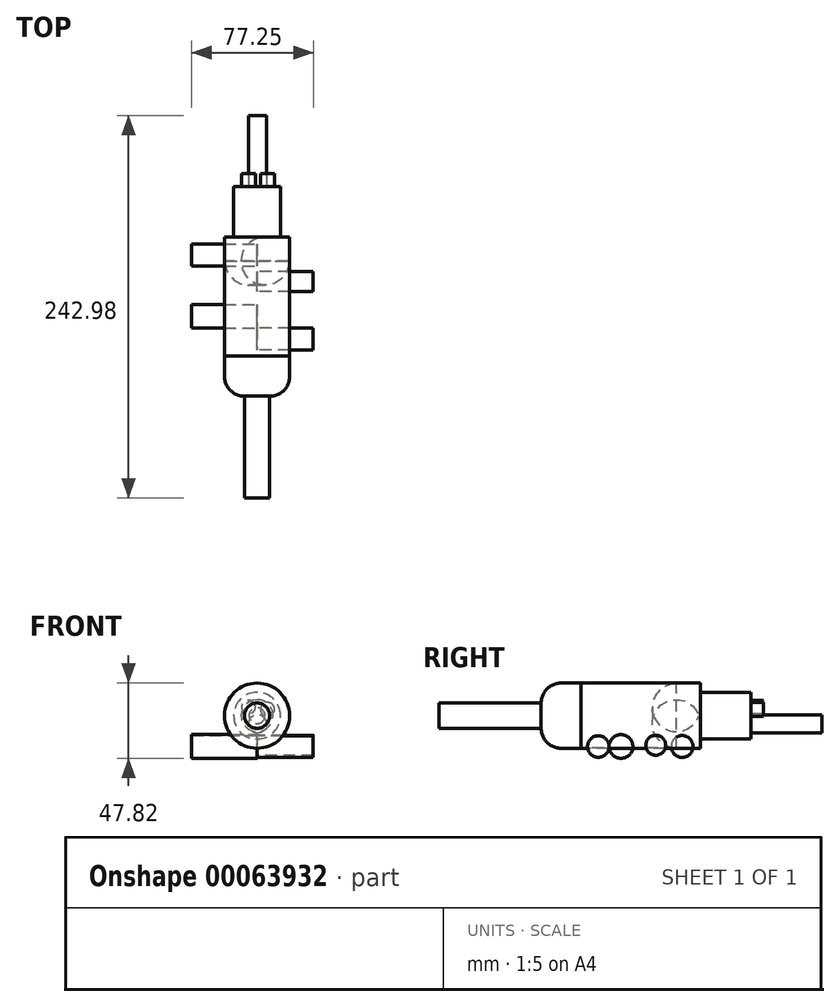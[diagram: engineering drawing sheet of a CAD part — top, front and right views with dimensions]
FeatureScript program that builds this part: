
annotation { "Feature Type Name" : "Feature", "Feature Type Description" : "" }
export const myFeature = defineFeature(function(context is Context, id is Id, definition is map)
    precondition{}
    {
        {
            var Q0;
            Q0=qCreatedBy(makeId("Front.planeOp"),FACE);
            var sketch = newSketch(context, id + "F0", { "sketchPlane" : qUnion([Q0])});
            skCircle(sketch, "E0", {"center": v(0, 0) * mm, "radius": 20.71 * mm});
            skSolve(sketch);
        }
        {
            var Q0;
            Q0 = qSketchRegion(id + "F0", true);
            extrude(context, id + "F1", {"entities" : qUnion([Q0]), "depth" : 25.4 * mm});
        }
        {
            var Q0;
            Q0=makeQuery(id+"F1.opExtrude","CAP_EDGE",EDGE,{"disambiguationData":[OSD([sQuery(id+"F0.wireOp",EDGE,"E0")])],"isStart":false});
            fillet(context, id + "F2", {"entities" : qUnion([Q0]), "radius" : 12.7 * mm, "tangentPropagation" : true, "allowEdgeOverflow" : false});
        }
        {
            var Q0;
            Q0=makeQuery(id+"F1.opExtrude","CAP_FACE",FACE,{"disambiguationData":[OSD([sQuery(id+"F0.wireOp",EDGE,"E0")])],"isStart":false});
            extrude(context, id + "F3", {"entities" : qUnion([Q0]), "depth" : 64.69 * mm});
        }
        {
            var Q0;
            Q0=qCreatedBy(makeId("Front.planeOp"),FACE);
            var sketch = newSketch(context, id + "F4", { "sketchPlane" : qUnion([Q0])});
            skCircle(sketch, "E1", {"center": v(0, 0) * mm, "radius": 20.32 * mm});
            skSolve(sketch);
        }
        {
            var Q0;
            Q0 = qSketchRegion(id + "F4", true);
            var Q1;
            Q1=makeQuery(id+"F1.opExtrude","CAP_FACE",FACE,{"disambiguationData":[OSD([sQuery(id+"F0.wireOp",EDGE,"E0")])],"isStart":true});
            extrude(context, id + "F5", {"entities" : qUnion([Q0, Q1]), "oppositeDirection" : true, "depth" : 75.69 * mm});
        }
        {
            var Q0;
            Q0=makeQuery(id+"F5.opExtrude","CAP_EDGE",EDGE,{"disambiguationData":[OSD([sQuery(id+"F4.wireOp",EDGE,"E1")])],"isStart":false});
            fillet(context, id + "F6", {"entities" : qUnion([Q0]), "radius" : 15.24 * mm, "tangentPropagation" : true, "allowEdgeOverflow" : false});
        }
        {
            var Q0;
            Q0=makeQuery(id+"F5.opExtrude","CAP_FACE",FACE,{"disambiguationData":[OSD([sQuery(id+"F0.wireOp",EDGE,"E0")])],"isStart":false});
            var sketch = newSketch(context, id + "F7", { "sketchPlane" : qUnion([Q0])});
            skCircle(sketch, "E2", {"center": v(0, 0) * mm, "radius": 14.85 * mm});
            skSolve(sketch);
        }
        {
            var Q0;
            Q0 = qSketchRegion(id + "F7", true);
            extrude(context, id + "F8", {"entities" : qUnion([Q0]), "depth" : 32.05 * mm});
        }
        {
            var Q0;
            Q0=makeQuery(id+"F8.opExtrude","CAP_FACE",FACE,{"disambiguationData":[OSD([sQuery(id+"F7.wireOp",EDGE,"E2")])],"isStart":false});
            var sketch = newSketch(context, id + "F9", { "sketchPlane" : qUnion([Q0])});
            skCircle(sketch, "E3", {"center": v(-6.64, 4) * mm, "radius": 4.4 * mm});
            skCircle(sketch, "E4", {"center": v(5.5, 5.38) * mm, "radius": 4.4 * mm});
            skSolve(sketch);
        }
        {
            var Q0;
            Q0 = qSketchRegion(id + "F9", true);
            extrude(context, id + "F10", {"entities" : qUnion([Q0]), "operationType" : NewBodyOperationType.ADD, "depth" : 8.15 * mm});
        }
        {
            var Q0;
            Q0=makeQuery(id+"F8.opExtrude","CAP_FACE",FACE,{"disambiguationData":[OSD([sQuery(id+"F7.wireOp",EDGE,"E2")])],"isStart":false});
            var sketch = newSketch(context, id + "F11", { "sketchPlane" : qUnion([Q0])});
            skCircle(sketch, "E5", {"center": v(-0.29, -5.12) * mm, "radius": 5.74 * mm});
            skPoint(sketch, "E5.first.point", {"position": v(-5.2, -2.15) * mm});
            skPoint(sketch, "E5.second.point", {"position": v(3.2, -9.68) * mm});
            skPoint(sketch, "E5.third.point", {"position": v(2.32, 0) * mm});
            skSolve(sketch);
        }
        {
            var Q0;
            Q0 = qSketchRegion(id + "F11", true);
            extrude(context, id + "F12", {"entities" : qUnion([Q0]), "operationType" : NewBodyOperationType.ADD, "depth" : 45.15 * mm});
        }
        {
            var Q0;
            Q0=qCreatedBy(makeId("Right.planeOp"),FACE);
            var sketch = newSketch(context, id + "F13", { "sketchPlane" : qUnion([Q0])});
            skCircle(sketch, "E6", {"center": v(47.44, -18.83) * mm, "radius": 6.34 * mm});
            skCircle(sketch, "E7", {"center": v(10.95, -19.63) * mm, "radius": 6.85 * mm});
            skSolve(sketch);
        }
        {
            var Q0;
            Q0 = qSketchRegion(id + "F13", true);
            extrude(context, id + "F14", {"entities" : qUnion([Q0]), "depth" : 35.69 * mm});
        }
        {
            var Q0;
            Q0=qCreatedBy(makeId("Right.planeOp"),FACE);
            var sketch = newSketch(context, id + "F15", { "sketchPlane" : qUnion([Q0])});
            skCircle(sketch, "E8", {"center": v(64.2, -19.56) * mm, "radius": 6.96 * mm});
            skCircle(sketch, "E9", {"center": v(25.33, -19.56) * mm, "radius": 7.55 * mm});
            skSolve(sketch);
        }
        {
            var Q0;
            Q0 = qSketchRegion(id + "F15", true);
            extrude(context, id + "F16", {"entities" : qUnion([Q0]), "oppositeDirection" : true, "depth" : 41.56 * mm});
        }
    });
